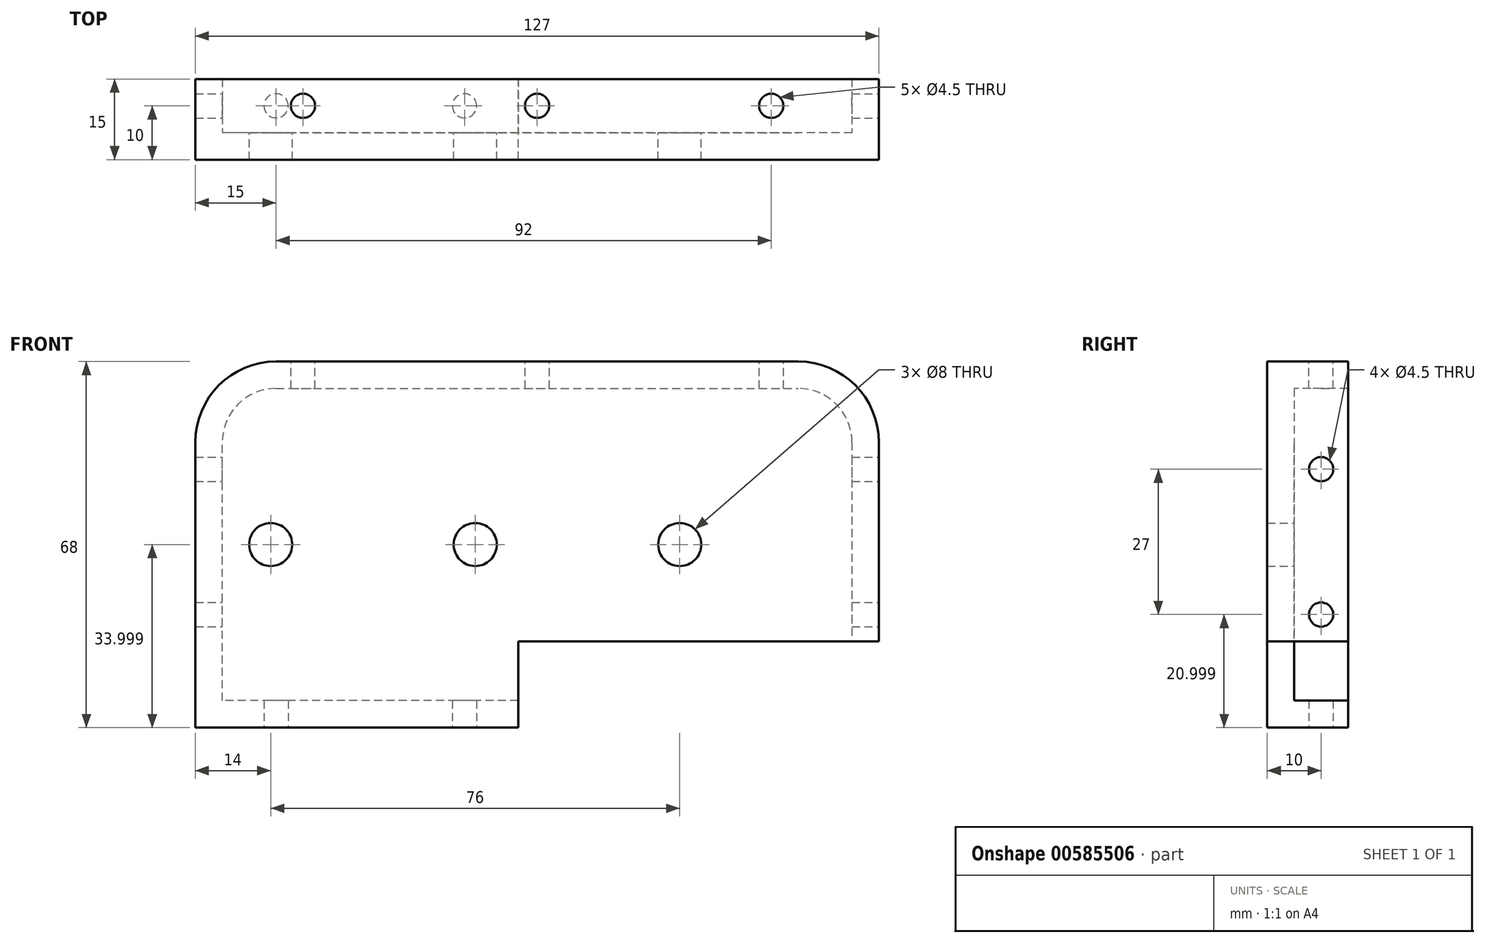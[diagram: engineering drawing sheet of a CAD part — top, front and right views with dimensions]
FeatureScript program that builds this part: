
annotation { "Feature Type Name" : "Feature", "Feature Type Description" : "" }
export const myFeature = defineFeature(function(context is Context, id is Id, definition is map)
    precondition{}
    {
        {
            var Q0;
            Q0=qCreatedBy(makeId("Front.planeOp"),FACE);
            var sketch = newSketch(context, id + "F0", { "sketchPlane" : qUnion([Q0])});
            skLineSegment(sketch, "E0.bottom", {"start": v(-52, 77.6) * mm, "end": v(75, 77.6) * mm});
            skLineSegment(sketch, "E0.top", {"start": v(-52, 9.6) * mm, "end": v(8, 9.6) * mm});
            skLineSegment(sketch, "E0.left", {"start": v(-52, 77.6) * mm, "end": v(-52, 9.6) * mm});
            skLineSegment(sketch, "E0.right", {"start": v(75, 77.6) * mm, "end": v(75, 25.6) * mm});
            skCircle(sketch, "E1", {"center": v(-38, 43.6) * mm, "radius": 4 * mm});
            skCircle(sketch, "E2", {"center": v(0, 43.6) * mm, "radius": 4 * mm});
            skCircle(sketch, "E3", {"center": v(38, 43.6) * mm, "radius": 4 * mm});
            skLineSegment(sketch, "E4", {"start": v(75, 25.6) * mm, "end": v(8, 25.6) * mm});
            skLineSegment(sketch, "E5", {"start": v(8, 25.6) * mm, "end": v(8, 9.6) * mm});
            skSolve(sketch);
        }
        {
            var Q0;
            Q0=makeQuery(id+"F0.imprint","IMPRINT",FACE,{"disambiguationData":[TD([[makeQuery(id+"F0.imprint","IMPRINT",EDGE,{"derivedFrom":sQuery(id+"F0.wireOp",EDGE,"E0.bottom")}),-1.0]])]});
            extrude(context, id + "F1", {"entities" : qUnion([Q0]), "depth" : 5 * mm, "offsetDistance" : 25 * mm});
        }
        {
            var Q0;
            Q0=makeQuery(id+"F1.opExtrude","CAP_FACE",FACE,{"disambiguationData":[OSD([sQuery(id+"F0.wireOp",EDGE,"E0.bottom"),sQuery(id+"F0.wireOp",EDGE,"E0.top"),sQuery(id+"F0.wireOp",EDGE,"E0.left"),sQuery(id+"F0.wireOp",EDGE,"E0.right"),sQuery(id+"F0.wireOp",EDGE,"E1"),sQuery(id+"F0.wireOp",EDGE,"E2"),sQuery(id+"F0.wireOp",EDGE,"E3"),sQuery(id+"F0.wireOp",EDGE,"E4"),sQuery(id+"F0.wireOp",EDGE,"E5")])],"isStart":true});
            var sketch = newSketch(context, id + "F2", { "sketchPlane" : qUnion([Q0])});
            skLineSegment(sketch, "E6", {"start": v(-75, 25.6) * mm, "end": v(-75, 77.6) * mm});
            skLineSegment(sketch, "E7", {"start": v(-75, 77.6) * mm, "end": v(52, 77.6) * mm});
            skLineSegment(sketch, "E8", {"start": v(52, 77.6) * mm, "end": v(52, 9.6) * mm});
            skLineSegment(sketch, "E9", {"start": v(52, 9.6) * mm, "end": v(-8, 9.6) * mm});
            skLineSegment(sketch, "E10", {"start": v(-8, 9.6) * mm, "end": v(-8, 14.6) * mm});
            skLineSegment(sketch, "E11", {"start": v(-8, 14.6) * mm, "end": v(47, 14.6) * mm});
            skLineSegment(sketch, "E12", {"start": v(47, 14.6) * mm, "end": v(47, 72.6) * mm});
            skLineSegment(sketch, "E13", {"start": v(47, 72.6) * mm, "end": v(-70, 72.6) * mm});
            skLineSegment(sketch, "E14", {"start": v(-70, 72.6) * mm, "end": v(-70, 25.6) * mm});
            skLineSegment(sketch, "E15", {"start": v(-70, 25.6) * mm, "end": v(-75, 25.6) * mm});
            skSolve(sketch);
        }
        {
            var Q0;
            Q0 = qSketchRegion(id + "F2", true);
            extrude(context, id + "F3", {"entities" : qUnion([Q0]), "operationType" : NewBodyOperationType.ADD, "depth" : 10 * mm, "offsetDistance" : 25 * mm});
        }
        {
            var Q0;
            Q0=makeQuery(id+"F3.boolean.opBoolean","MERGE",FACE,{"derivedFrom":[makeQuery(id+"F1.opExtrude","SWEPT_FACE",FACE,{"disambiguationData":[OSD([sQuery(id+"F0.wireOp",EDGE,"E0.top")])]}),makeQuery(id+"F3.opExtrude","SWEPT_FACE",FACE,{"disambiguationData":[OSD([sQuery(id+"F2.wireOp",EDGE,"E9")])]})]});
            var sketch = newSketch(context, id + "F4", { "sketchPlane" : qUnion([Q0])});
            skCircle(sketch, "E16", {"center": v(-37, -5) * mm, "radius": 2.25 * mm});
            skCircle(sketch, "E17", {"center": v(-2, -5) * mm, "radius": 2.25 * mm});
            skSolve(sketch);
        }
        {
            var Q0;
            Q0 = qSketchRegion(id + "F4", true);
            extrude(context, id + "F5", {"entities" : qUnion([Q0]), "operationType" : NewBodyOperationType.REMOVE, "endBound" : BoundingType.UP_TO_NEXT, "oppositeDirection" : true, "depth" : 25 * mm, "offsetDistance" : 25 * mm});
        }
        {
            var Q0;
            Q0=makeQuery(id+"F3.boolean.opBoolean","MERGE",FACE,{"derivedFrom":[makeQuery(id+"F1.opExtrude","SWEPT_FACE",FACE,{"disambiguationData":[OSD([sQuery(id+"F0.wireOp",EDGE,"E0.right")])]}),makeQuery(id+"F3.opExtrude","SWEPT_FACE",FACE,{"disambiguationData":[OSD([sQuery(id+"F2.wireOp",EDGE,"E6")])]})]});
            var sketch = newSketch(context, id + "F6", { "sketchPlane" : qUnion([Q0])});
            skCircle(sketch, "E18", {"center": v(5, 30.6) * mm, "radius": 2.25 * mm});
            skCircle(sketch, "E19", {"center": v(5, 57.6) * mm, "radius": 2.25 * mm});
            skSolve(sketch);
        }
        {
            var Q0;
            Q0 = qSketchRegion(id + "F6", true);
            extrude(context, id + "F7", {"entities" : qUnion([Q0]), "operationType" : NewBodyOperationType.REMOVE, "endBound" : BoundingType.THROUGH_ALL, "oppositeDirection" : true, "depth" : 25 * mm, "offsetDistance" : 25 * mm});
        }
        {
            var Q0;
            Q0=makeQuery(id+"F3.boolean.opBoolean","MERGE",FACE,{"derivedFrom":[makeQuery(id+"F1.opExtrude","SWEPT_FACE",FACE,{"disambiguationData":[OSD([sQuery(id+"F0.wireOp",EDGE,"E0.bottom")])]}),makeQuery(id+"F3.opExtrude","SWEPT_FACE",FACE,{"disambiguationData":[OSD([sQuery(id+"F2.wireOp",EDGE,"E7")])]})]});
            var sketch = newSketch(context, id + "F8", { "sketchPlane" : qUnion([Q0])});
            skCircle(sketch, "E20", {"center": v(55, 5) * mm, "radius": 2.25 * mm});
            skCircle(sketch, "E21", {"center": v(11.5, 5) * mm, "radius": 2.25 * mm});
            skCircle(sketch, "E22", {"center": v(-32, 5) * mm, "radius": 2.25 * mm});
            skSolve(sketch);
        }
        {
            var Q0;
            Q0 = qSketchRegion(id + "F8", true);
            extrude(context, id + "F9", {"entities" : qUnion([Q0]), "operationType" : NewBodyOperationType.REMOVE, "endBound" : BoundingType.UP_TO_NEXT, "oppositeDirection" : true, "depth" : 25 * mm, "offsetDistance" : 25 * mm});
        }
        {
            var Q0;
            Q0=makeQuery(id+"F3.opExtrude","SWEPT_EDGE",EDGE,{"disambiguationData":[OSD([sQuery(id+"F2.wireOp",EDGE,"E13"),sQuery(id+"F2.wireOp",EDGE,"E14")])]});
            var Q1;
            Q1=makeQuery(id+"F3.opExtrude","SWEPT_EDGE",EDGE,{"disambiguationData":[OSD([sQuery(id+"F2.wireOp",EDGE,"E12"),sQuery(id+"F2.wireOp",EDGE,"E13")])]});
            fillet(context, id + "F10", {"entities" : qUnion([Q0, Q1]), "radius" : 10 * mm, "tangentPropagation" : true, "allowEdgeOverflow" : false});
        }
        {
            var Q0;
            Q0=makeQuery(id+"F3.boolean.opBoolean","MERGE",EDGE,{"derivedFrom":[makeQuery(id+"F1.opExtrude","SWEPT_EDGE",EDGE,{"disambiguationData":[OSD([sQuery(id+"F0.wireOp",EDGE,"E0.bottom"),sQuery(id+"F0.wireOp",EDGE,"E0.right")])]}),makeQuery(id+"F3.opExtrude","SWEPT_EDGE",EDGE,{"disambiguationData":[OSD([sQuery(id+"F2.wireOp",EDGE,"E6"),sQuery(id+"F2.wireOp",EDGE,"E7")])]})]});
            var Q1;
            Q1=makeQuery(id+"F3.boolean.opBoolean","MERGE",EDGE,{"derivedFrom":[makeQuery(id+"F1.opExtrude","SWEPT_EDGE",EDGE,{"disambiguationData":[OSD([sQuery(id+"F0.wireOp",EDGE,"E0.bottom"),sQuery(id+"F0.wireOp",EDGE,"E0.left")])]}),makeQuery(id+"F3.opExtrude","SWEPT_EDGE",EDGE,{"disambiguationData":[OSD([sQuery(id+"F2.wireOp",EDGE,"E7"),sQuery(id+"F2.wireOp",EDGE,"E8")])]})]});
            fillet(context, id + "F11", {"entities" : qUnion([Q0, Q1]), "radius" : 15 * mm, "tangentPropagation" : true, "allowEdgeOverflow" : false});
        }
    });
